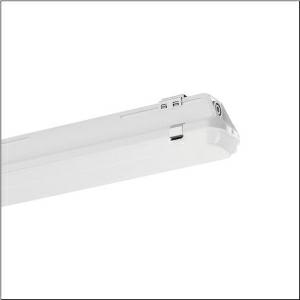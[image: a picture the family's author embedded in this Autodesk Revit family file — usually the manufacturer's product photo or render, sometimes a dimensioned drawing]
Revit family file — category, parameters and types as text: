
# Revit family: monsun_11_51fp20dp460l007
name_source: partatom
category: Lighting Fixtures
units: mm (PartAtom-declared; Revit-internal decimal feet)

## family parameters
Cut with Voids When Loaded = No
Host = Face
Light Source = No
Part Type = Normal
Room Calculation Point = No
Round Connector Dimension = Use Diameter
Shared = No

## types (1)
- --- (1 x LED, 5450 lm, 31.5 W, 4000K)
    Apparent Load = 32 VA
    CIE Flux Codes = 45 75 93 94 100
    Color Rendering = 80
    Color Temperature = 4000K
    Default Elevation = 1800 mm
    Description = Monsun 11, damp-proof luminaire, chain hanger, primary optical cover: enclosure, of PC, light emission: direct distribution, primary light characteristic: symmetric, installation type: suspended mounting, surface-mounted, horizontal mounting, vertical mounting, LED, rated luminous flux: 5.450lm, luminous efficacy: 173lm/W, light colour: 840, colour temperature: 4000K, control gear: DALI 2, with terminal, 5-pole, max. 2.5mm², through-wiring: 7x 2.5mm², mains connection: 220..240V, AC, 50/60Hz, rated input power: 32W, housing, of glass-fibre reinforced polyester, uncoated, bright grey, incl. chain hanger, length: 1.590mm, width: 90mm, height: 88mm, clip for enclosure, of stainless steel (V2A), ceiling mounting element, of stainless steel (V2A), chain hanger, of stainless steel (V2A), protection rating (complete): IP66, insulation class (complete): insulation class I (protective earthing), certification: CE, ENEC, VDE, UKCA, protection symbol: D, impact resistance: IK08, permissible operating ambient temperature: -25..+30°C, standard: EN 50419, EN 60598-2-1, corresponds to IFS (International Featured Standards) requirements for safety and quality in the food industry, for indoor or canopied outdoor use, no direct snow, no direct sun, no direct rain, LABS conformity tested according to VDMA 24364:2018-05, contact your sales advisor before using the luminaires in applications with unclear chemical exposure, large temperature fluctuations or condensation-forming humidity, packaging unit: 1 piece
    Height = 89 mm
    Lamp = 1 x LED
    Lamp Light Flux = 5450 lm
    Lamp Power = 31.5 W
    Lamp count = 1
    Length = 1590 mm
    Luminous efficacy = 173 lm/W
    Manufacturer = Siteco
    ModVariant = No
    Model = 51FP20DP460L007
    Mounting Place = Ceiling
    Mounting Type = Surface mounted
    Number of Poles = 1
    OnlyDefault = Yes
    Power Factor = 1
    Product Name = Monsun 11
    Product group = damp-proof luminaire
    ProductGroupID = 300
    Protection Class = Protection class I
    Protection Degree = IP 66
    RLX_Detail_Level = 1
    RLX_Emergency_Light_Flux = 0 lm
    RLX_Emergency_Type = 0
    RLX_Emergency_Type_DB = No
    RlxData = <blob elided: 92329 chars, md5=3044ec85>
    Socket = socket
    Standby Power = 0 W
    System Light Flux = 5450 lm
    System Power = 32 W
    Type Comments = factory setting: luminous flux: 100 % | dim-lin: 254 | 219 mA
    Type Image = l_1349237.jpg
    URL = http://relux.com
    VarID = @adj_034205
    Voltage = 0 V
    Weight = 0.00 kg
    Width = 90 mm

## geometry (parser evidence)
native form markers: Blend x4, Sweep x14
no freeform markers — native parametric forms only
